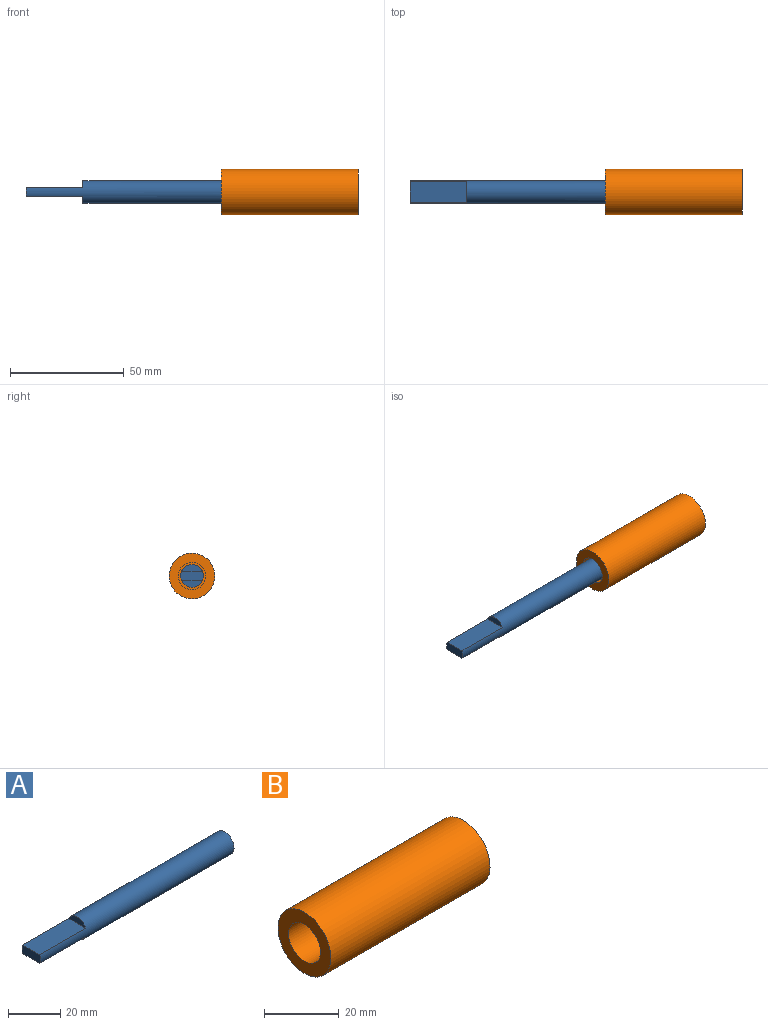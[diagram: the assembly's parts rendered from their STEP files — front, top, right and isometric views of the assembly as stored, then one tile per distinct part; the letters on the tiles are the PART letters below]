
ASSEMBLY  parts=2 mates=1
PART A: 7 faces, bbox 105x10x10 mm
  f0: plane 9.17x3mm, normal (-1,0,0), area 19.8mm2, adj f1,f4
  f1: cylinder r=5mm len=105mm, axis (-1,0,0), area 2719mm2, adj f0,f2,f3,f4,f5,f6
  f2: plane 9.17x3mm, normal (-1,0,0), area 19.8mm2, adj f1,f5
  f3: plane 10x10mm, normal (1,0,0), area 78.5mm2, adj f1
  f4: plane 25x9.17mm, normal (0,0,1), area 229.1mm2, adj f0,f1,f6
  f5: plane 25x9.17mm, normal (0,0,-1), area 229.1mm2, adj f1,f2,f6
  f6: plane 10x4mm, normal (-1,0,0), area 38.9mm2, adj f1,f4,f5
PART B: 5 faces, bbox 60x20x20 mm
  f0: plane 20x20mm, normal (1,0,0), area 314.2mm2, adj f1
  f1: cylinder r=10mm len=60mm, axis (-1,0,0), area 3769.9mm2, adj f0,f2
  f2: plane 20x20mm, normal (-1,0,0), area 201.1mm2, adj f1,f3
  f3: cylinder r=6mm len=56mm, axis (-1,0,0), area 2111.2mm2, adj f2,f4
  f4: plane 12x12mm, normal (-1,0,0), area 113.1mm2, adj f3
PLACE A t=(2.5,0,0)mm
PLACE B rot(axis=(-1,0,0),25.5deg) t=(33.14,0,0)mm
MATE cylindrical B.f1 <-> A.f1  axis (-1,0,0) through (33.14,0,0)mm
